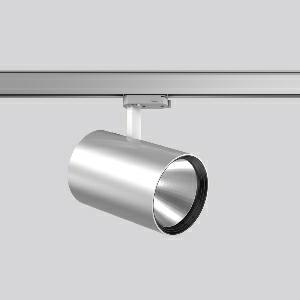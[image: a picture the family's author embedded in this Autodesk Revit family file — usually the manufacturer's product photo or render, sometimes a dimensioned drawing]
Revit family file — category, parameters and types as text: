
# Revit family: deecos_s_maxi_742221_004_1_76_da4f
name_source: partatom
category: Lighting Fixtures
units: mm (PartAtom-declared; Revit-internal decimal feet)

## family parameters
Cut with Voids When Loaded = No
Host = Face
Light Source = No
Part Type = Normal
Room Calculation Point = No
Round Connector Dimension = Use Diameter
Shared = No

## types (1)
- DEECOS S maxi (1 x LED Modul 940, 4550 lm, 4000)
    Apparent Load = 35 VA
    Approval mark = CE
    CIE Flux Codes = 100 100 100 100 100
    Color Rendering = 92
    Color Temperature = 4000
    Default Elevation = 1800 mm
    Description = Series: DEECOS S maxi
LED surface-mounted projector in modern design with no visible cooling ribs. Housing: die-cast aluminium, powder-coated. Rotation range: 356°. Swivel range: 90°. Black plastic ring and recessed LED to prevent glare from the side. Optical assembly with reflector made of MIRO-Silver with 98% total light reflection for outstanding efficiency - can be changed without tools. Best colour rendering index Ra>90. With adapter for RZB 3-circuit DALI tracks. Suitable for Track on ceiling, Wall track. High quality converter without flickering and stroboscopic effect. The following accessories can be mounted without use of tools: interchangeable lenses, decorative glasses, honeycomb louvre, clear and frosted diffusers, white interchangeable plastic ring. 
Colour: silver
Diameter: 123 mm
Height: 200 mm
Lamp: LED
Socket: without socket
Colour temperature: 4000K
Colour rendering index (CRI): 92
System power: 35 W
Rated luminous flux: 4550 lm
Luminous efficiency: 130 lm/W
Control gear: Converter, dimmable, DALI
Protection class: I
Type of protection: IP 20
    Height = 200 mm  [stored 0.656168 ft]
    Lamp = 1 x LED Modul 940
    Lamp Light Flux = 4550 lm
    Lamp count = 1
    Length = 123 mm
    Lifetime = 50000 h
    Luminous efficacy = 130 lm/W
    Manufacturer = RZB
    ModVariant = No
    Model = 742221.004.1.76
    Mounting Place = Ceiling
    Mounting Type = Rail mounted
    Number of Poles = 1
    OnlyDefault = Yes
    Power Factor = 1
    Product Name = DEECOS S maxi
    Product group = Track mounted projectors
    ProductGroupID = 301
    Protection Class = Protection class I
    Protection Degree = IP 20
    RLX_Detail_Level = 1
    RLX_Emergency_Light_Flux = 0 lm
    RLX_Emergency_Type = 0
    RLX_Emergency_Type_DB = No
    RlxData = <blob elided: 40109 chars, md5=2546ab58>
    Socket = socket
    Standby Power = 0 W
    System Light Flux = 4550 lm
    System Power = 35 W
    Type Comments = Product without accessories
    Type Image = 741954.004.jpg
    URL = http://relux.com
    VarID = ---
    Voltage = 230 V
    Voltage Range = 220-240 V
    Weight = 0.00 kg
    Width = 0 mm  [stored 0 ft]

note: [stored X ft] marks values corroborated as IEEE doubles in the binary element streams (Revit-internal decimal feet)

## geometry (parser evidence)
native form markers: Blend x4, Sweep x13
no freeform markers — native parametric forms only
